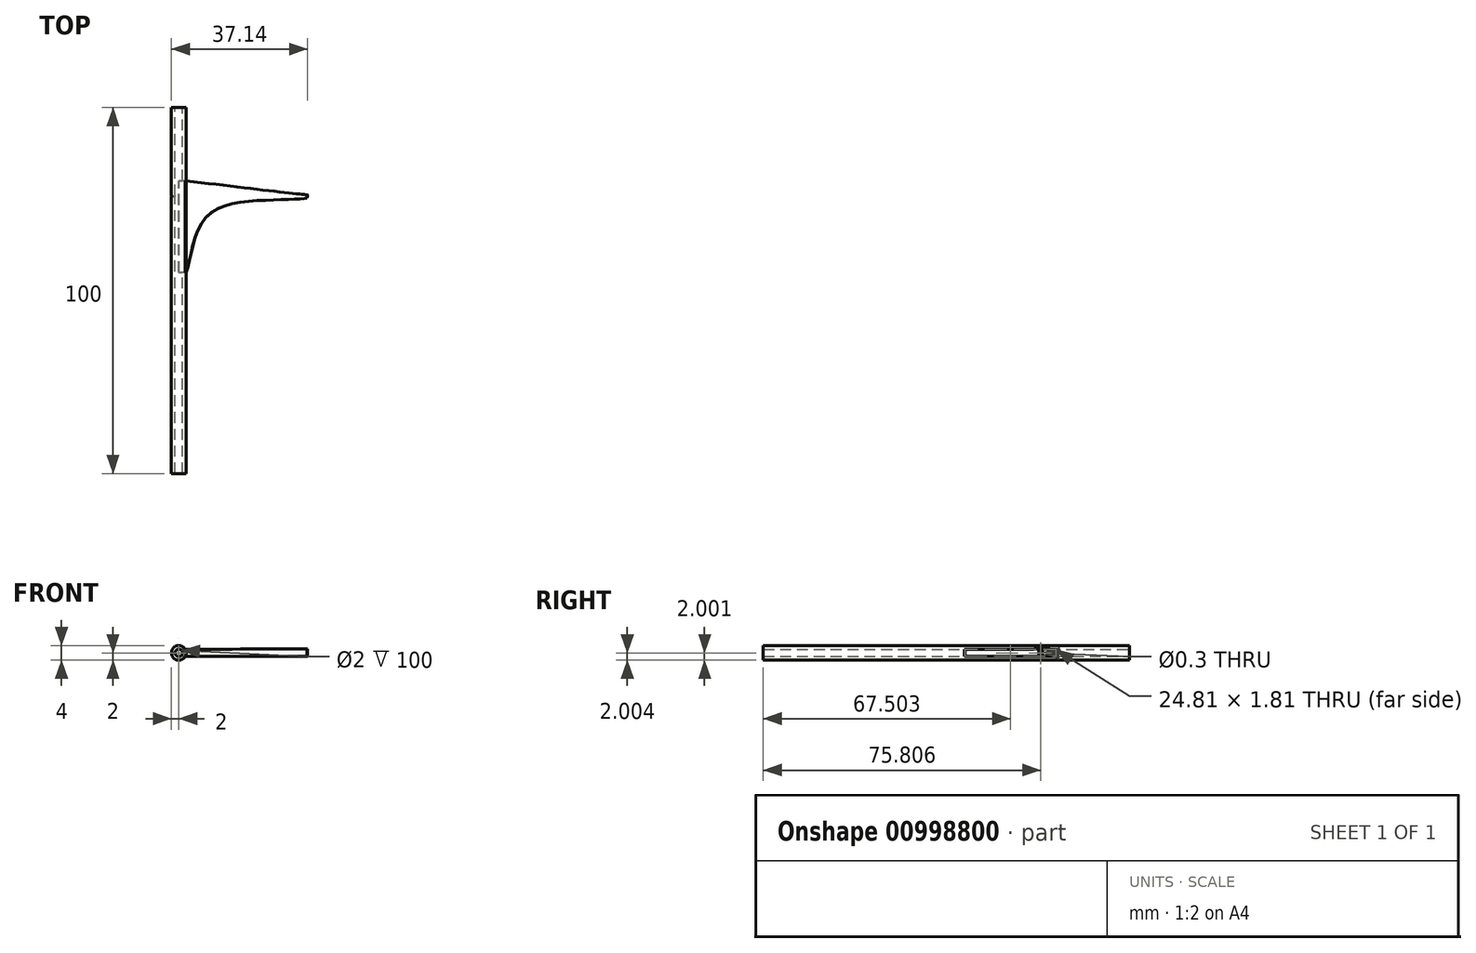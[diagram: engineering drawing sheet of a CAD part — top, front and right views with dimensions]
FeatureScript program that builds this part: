
annotation { "Feature Type Name" : "Feature", "Feature Type Description" : "" }
export const myFeature = defineFeature(function(context is Context, id is Id, definition is map)
    precondition{}
    {
        {
            var Q0;
            Q0=qCreatedBy(makeId("Front.planeOp"),FACE);
            var sketch = newSketch(context, id + "F0", { "sketchPlane" : qUnion([Q0])});
            skCircle(sketch, "E0", {"center": v(0, 0) * mm, "radius": 1 * mm});
            skCircle(sketch, "E1.0", {"center": v(0, 0) * mm, "radius": 2 * mm});
            skPoint(sketch, "E2", {"position": v(0, -1) * mm});
            skSolve(sketch);
        }
        {
            var Q0;
            Q0=qSketchRegion(id+"F0",true);
            extrude(context, id + "F1", {"entities" : qUnion([Q0]), "depth" : 100 * mm, "offsetDistance" : 25 * mm});
        }
        {
            var Q0;
            Q0=sQuery(id+"F0.wireOp",VERTEX,"E2");
            var Q1;
            Q1=sQuery(id+"F0.wireOp",EDGE,"E0");
            cPlane(context, id + "F2", {"entities" : qUnion([Q0, Q1]), "cplaneType" : CPlaneType.LINE_POINT, "offset" : 25 * mm, "width" : 150 * mm, "height" : 150 * mm});
        }
        {
            var Q0;
            Q0=qCreatedBy(id+"F2.planeOp",FACE);
            cPlane(context, id + "F3", {"entities" : qUnion([Q0]), "cplaneType" : CPlaneType.OFFSET, "offset" : 45 * mm, "width" : 150 * mm, "height" : 150 * mm});
        }
        {
            var Q0;
            Q0=qCreatedBy(id+"F3.planeOp",FACE);
            var sketch = newSketch(context, id + "F4", { "sketchPlane" : qUnion([Q0])});
            skLineSegment(sketch, "E3", {"start": v(0, -1) * mm, "end": v(1, -1) * mm, "construction": true});
            skLineSegment(sketch, "E4", {"start": v(0, 1) * mm, "end": v(1, 1) * mm, "construction": true});
            skLineSegment(sketch, "E5", {"start": v(1, -1) * mm, "end": v(1, 1) * mm});
            skSolve(sketch);
        }
        {
            var Q0;
            Q0=qSketchRegion(id+"F4",true);
            var Q1;
            Q1=sQuery(id+"F4.wireOp",EDGE,"E5");
            extrude(context, id + "F5", {"entities" : qUnion([Q0]), "bodyType" : ToolBodyType.SURFACE, "operationType" : NewBodyOperationType.REMOVE, "surfaceEntities" : qUnion([Q1]), "oppositeDirection" : true, "depth" : 25 * mm, "offsetDistance" : 25 * mm});
        }
        {
            var Q0;
            Q0=makeQuery(id+"F5.opExtrude","SWEPT_FACE",FACE,{"disambiguationData":[OSD([sQuery(id+"F4.wireOp",EDGE,"E5")])]});
            extrude(context, id + "F6", {"entities" : qUnion([Q0]), "operationType" : NewBodyOperationType.REMOVE, "oppositeDirection" : true, "depth" : 25 * mm, "offsetDistance" : 25 * mm, "hasSecondDirection" : true, "secondDirectionOppositeDirection" : false, "secondDirectionDepth" : 1 * mm});
        }
        {
            var Q0;
            Q0=makeQuery(id+"F6.boolean.opBoolean","INTERSECT",EDGE,{"derivedFrom":[makeQuery(id+"F1.opExtrude","SWEPT_FACE",FACE,{"disambiguationData":[OSD([sQuery(id+"F0.wireOp",EDGE,"E1.0")])]}),makeQuery(id+"F6.opExtrude","SWEPT_FACE",FACE,{"disambiguationData":[OSD([sQuery(id+"F4.wireOp",VERTEX,"E5.start")])]})]});
            var Q1;
            Q1=makeQuery(id+"F6.boolean.opBoolean","INTERSECT",EDGE,{"derivedFrom":[makeQuery(id+"F1.opExtrude","SWEPT_FACE",FACE,{"disambiguationData":[OSD([sQuery(id+"F0.wireOp",EDGE,"E1.0")])]}),makeQuery(id+"F6.opExtrude","SWEPT_FACE",FACE,{"disambiguationData":[OSD([sQuery(id+"F4.wireOp",VERTEX,"E5.end")])]})]});
            cPlane(context, id + "F7", {"entities" : qUnion([Q0, Q1]), "cplaneType" : CPlaneType.LINE_ANGLE, "offset" : 25 * mm, "angle" : 0 * degree, "width" : 150 * mm, "height" : 150 * mm});
        }
        {
            var Q0;
            Q0=qCreatedBy(id+"F7.planeOp",FACE);
            var sketch = newSketch(context, id + "F8", { "sketchPlane" : qUnion([Q0])});
            skLineSegment(sketch, "E6.bottom", {"start": v(-20, -1) * mm, "end": v(-45, -1) * mm});
            skLineSegment(sketch, "E6.top", {"start": v(-20, 1) * mm, "end": v(-45, 1) * mm});
            skLineSegment(sketch, "E6.left", {"start": v(-20, -1) * mm, "end": v(-20, 1) * mm});
            skLineSegment(sketch, "E6.right", {"start": v(-45, -1) * mm, "end": v(-45, 1) * mm});
            skLineSegment(sketch, "E7", {"start": v(-45, 0) * mm, "end": v(-20, 0) * mm});
            skLineSegment(sketch, "E8", {"start": v(-45, 0) * mm, "end": v(-41.17, 0) * mm});
            skLineSegment(sketch, "E9", {"start": v(-20, 0) * mm, "end": v(-24.2, 0) * mm});
            skSolve(sketch);
        }
        {
            var Q0;
            Q0=qSketchRegion(id+"F8",true);
            extrude(context, id + "F9", {"entities" : qUnion([Q0]), "depth" : 0.3 * mm, "offsetDistance" : 25 * mm});
        }
        {
            var Q0;
            Q0=makeQuery(id+"F9.opExtrude","CAP_FACE",FACE,{"disambiguationData":[OSD([sQuery(id+"F8.wireOp",EDGE,"E6.bottom"),sQuery(id+"F8.wireOp",EDGE,"E6.top"),sQuery(id+"F8.wireOp",EDGE,"E6.left"),sQuery(id+"F8.wireOp",EDGE,"E6.right")])],"isStart":false});
            var Q1;
            Q1=makeQuery(id+"F9.opExtrude","CAP_FACE",FACE,{"disambiguationData":[OSD([sQuery(id+"F8.wireOp",EDGE,"E6.bottom"),sQuery(id+"F8.wireOp",EDGE,"E6.top"),sQuery(id+"F8.wireOp",EDGE,"E6.left"),sQuery(id+"F8.wireOp",EDGE,"E6.right")])],"isStart":true});
            var Q2;
            Q2=makeQuery(id+"F9.opExtrude","SWEPT_BODY",BODY,{"disambiguationData":[OSD([sQuery(id+"F8.wireOp",EDGE,"E6.bottom"),sQuery(id+"F8.wireOp",EDGE,"E6.top"),sQuery(id+"F8.wireOp",EDGE,"E6.left"),sQuery(id+"F8.wireOp",EDGE,"E6.right")])]});
            shell(context, id + "F10", {"entities" : qUnion([Q0, Q1]), "parts" : qUnion([Q2]), "thickness" : 0.1 * mm});
        }
        {
            var Q0;
            Q0=makeQuery(id+"F9.opExtrude","SWEPT_FACE",FACE,{"disambiguationData":[OSD([sQuery(id+"F8.wireOp",EDGE,"E6.bottom")])]});
            var sketch = newSketch(context, id + "F11", { "sketchPlane" : qUnion([Q0])});
            skFitSpline(sketch, "E10", {"points": [v(2.03, 45) * mm, v(7.48, 29.95) * mm, v(25.31, 25.25) * mm, v(34.98, 24.78) * mm], "startDerivative": vector(10.95, -31.1) * mm, "endDerivative": vector(12.07, -2.32) * mm});
            skFitSpline(sketch, "E11", {"points": [v(2.03, 20) * mm, v(35.03, 23.77) * mm, v(34.98, 23.74) * mm], "startDerivative": vector(51.53, 6.22) * mm, "endDerivative": vector(-2, -0.91) * mm});
            skLineSegment(sketch, "E12", {"start": v(34.98, 24.78) * mm, "end": v(35.03, 23.77) * mm});
            skSolve(sketch);
        }
        {
            var Q0;
            Q0=makeQuery(id+"F11.imprint","IMPRINT",FACE,{"disambiguationData":[TD([[makeQuery(id+"F11.imprint","IMPRINT",EDGE,{"derivedFrom":sQuery(id+"F11.wireOp",EDGE,"E10")}),-1.0]])]});
            extrude(context, id + "F12", {"entities" : qUnion([Q0]), "oppositeDirection" : true, "depth" : 2 * mm, "offsetDistance" : 25 * mm});
        }
        {
            var Q0;
            Q0=makeQuery(id+"F12.opExtrude","SWEPT_FACE",FACE,{"disambiguationData":[OSD([sQuery(id+"F11.wireOp",EDGE,"E12")])]});
            var Q1;
            Q1=makeQuery(id+"F12.opExtrude","SWEPT_FACE",FACE,{"disambiguationData":[OSD([sQuery(id+"F8.wireOp",EDGE,"E6.bottom")])]});
            shell(context, id + "F13", {"entities" : qUnion([Q0, Q1]), "thickness" : 0.1 * mm});
        }
        {
            var Q0;
            Q0=makeQuery(id+"F12.opExtrude","SWEPT_FACE",FACE,{"disambiguationData":[OSD([sQuery(id+"F11.wireOp",EDGE,"E12")])]});
            var sketch = newSketch(context, id + "F14", { "sketchPlane" : qUnion([Q0])});
            skLineSegment(sketch, "E13.bottom", {"start": v(-22.83, 0.9) * mm, "end": v(-22.04, 0.9) * mm});
            skLineSegment(sketch, "E13.top", {"start": v(-22.83, -0.9) * mm, "end": v(-22.04, -0.9) * mm});
            skLineSegment(sketch, "E13.left", {"start": v(-22.83, 0.9) * mm, "end": v(-22.83, -0.9) * mm});
            skLineSegment(sketch, "E13.right", {"start": v(-22.04, 0.9) * mm, "end": v(-22.04, -0.9) * mm});
            skLineSegment(sketch, "E14", {"start": v(-22.43, 0.9) * mm, "end": v(-22.43, -0.9) * mm});
            skLineSegment(sketch, "E15", {"start": v(-22.43, -0.9) * mm, "end": v(-22.43, 0) * mm});
            skLineSegment(sketch, "E16.bottom", {"start": v(-22.94, 1) * mm, "end": v(-21.93, 1) * mm});
            skLineSegment(sketch, "E16.top", {"start": v(-22.94, -1) * mm, "end": v(-21.93, -1) * mm});
            skLineSegment(sketch, "E16.left", {"start": v(-22.94, 1) * mm, "end": v(-22.94, -1) * mm});
            skLineSegment(sketch, "E16.right", {"start": v(-21.93, 1) * mm, "end": v(-21.93, -1) * mm});
            skSolve(sketch);
        }
        {
            var Q0;
            {var subQ4=sQuery(id+"F14.wireOp",EDGE,"E13.left");Q0=makeQuery(id+"F14.imprint","IMPRINT",FACE,{"disambiguationData":[TD([[makeQuery(id+"F14.imprint","IMPRINT",EDGE,{"derivedFrom":subQ4}),-1.0]])]});}
            var Q1;
            {var subQ4=sQuery(id+"F14.wireOp",EDGE,"E13.left");Q1=makeQuery(id+"F14.imprint","IMPRINT",FACE,{"disambiguationData":[TD([[makeQuery(id+"F14.imprint","IMPRINT",EDGE,{"derivedFrom":subQ4}),1.0]])]});}
            var Q2;
            {var subQ0=sQuery(id+"F14.wireOp",EDGE,"E13.right");Q2=makeQuery(id+"F14.imprint","IMPRINT",FACE,{"disambiguationData":[TD([[makeQuery(id+"F14.imprint","IMPRINT",EDGE,{"derivedFrom":subQ0}),-1.0]])]});}
            extrude(context, id + "F15", {"entities" : qUnion([Q0, Q1, Q2]), "depth" : 0.1 * mm, "offsetDistance" : 25 * mm});
        }
        {
            var Q0;
            Q0=sQuery(id+"F14.wireOp",VERTEX,"E15.end");
            var Q1;
            Q1=makeQuery(id+"F15.opExtrude","SWEPT_BODY",BODY,{"disambiguationData":[OSD([sQuery(id+"F14.wireOp",EDGE,"E13.bottom"),sQuery(id+"F14.wireOp",EDGE,"E13.top"),sQuery(id+"F14.wireOp",EDGE,"E13.left"),sQuery(id+"F14.wireOp",EDGE,"E13.right")])]});
            var Q2;
            Q2=makeQuery(id+"F15.opExtrude","SWEPT_BODY",BODY,{"disambiguationData":[OSD([sQuery(id+"F14.wireOp",EDGE,"E16.bottom"),sQuery(id+"F14.wireOp",EDGE,"E16.top"),sQuery(id+"F14.wireOp",EDGE,"E16.left"),sQuery(id+"F14.wireOp",EDGE,"E16.right")])]});
            hole(context, id + "F16", {"style" : HoleStyle.SIMPLE, "endStyle" : HoleEndStyle.THROUGH, "oppositeDirection" : true, "holeDiameter" : 0.3 * mm, "majorDiameter" : 5 * mm, "isTappedThrough" : true, "tappedDepth" : 12 * mm, "tapClearance" : 3, "locations" : qUnion([Q0]), "scope" : qUnion([Q1, Q2])});
        }
        {
            var Q0;
            Q0=sQuery(id+"F8.wireOp",VERTEX,"E9.end");
            var Q1;
            Q1=makeQuery(id+"F1.opExtrude","SWEPT_BODY",BODY,{"disambiguationData":[OSD([sQuery(id+"F0.wireOp",EDGE,"E0"),sQuery(id+"F0.wireOp",EDGE,"E1.0")])]});
            hole(context, id + "F17", {"style" : HoleStyle.SIMPLE, "endStyle" : HoleEndStyle.THROUGH, "holeDiameter" : 0.3 * mm, "majorDiameter" : 5 * mm, "isTappedThrough" : true, "tappedDepth" : 12 * mm, "tapClearance" : 3, "locations" : qUnion([Q0]), "scope" : qUnion([Q1])});
        }
    });
